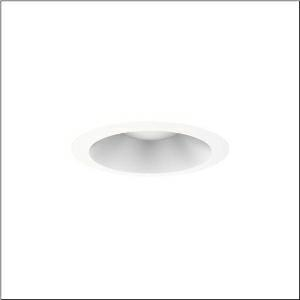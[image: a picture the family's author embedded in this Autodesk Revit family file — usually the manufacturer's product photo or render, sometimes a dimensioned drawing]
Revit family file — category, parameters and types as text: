
# Revit family: lunis_31-xl_51dn15eg42b
name_source: partatom
category: Lighting Fixtures
units: mm (PartAtom-declared; Revit-internal decimal feet)

## family parameters
Cut with Voids When Loaded = No
Host = Face
Light Source = No
Part Type = Normal
Room Calculation Point = No
Round Connector Dimension = Use Diameter
Shared = No

## types (1)
- --- (1 x LED, 2500 lm, 17.5 W, 4000K)
    Apparent Load = 18 VA
    CIE Flux Codes = 89 99 100 100 100
    Color Rendering = 80
    Color Temperature = 4000K
    Default Elevation = 1800 mm
    Description = Lunis 31-XL, downlight, light control with lens, light emission: direct distribution, LED rated luminous flux: 2.500lm, light colour: 840, mains connection: 220..240V, AC/DC, 0/50..60Hz, housing, of aluminium, white, protection rating (complete): IP20, protection rating (on room side): IP54, insulation class (complete): insulation class II (safety insulation), certification: CE, ENEC, packaging unit: 1 piece
    Height = 0 mm  [stored 0 ft]
    Lamp = 1 x LED
    Lamp Light Flux = 2500 lm
    Lamp Power = 17.5 W
    Lamp count = 1
    Length = 259 mm
    Luminous efficacy = 143 lm/W
    Manufacturer = Siteco
    ModVariant = No
    Model = 51DN15EG42B
    Mounting Place = Ceiling
    Mounting Type = Recessed
    Number of Poles = 1
    OnlyDefault = Yes
    Power Factor = 1
    Product Name = Lunis 31-XL
    Product group = downlight
    ProductGroupID = 401
    Protection Class = Protection class II
    Protection Degree = IP 20
    RLX_Detail_Level = 1
    RLX_Emergency_Light_Flux = 0 lm
    RLX_Emergency_Type = 0
    RLX_Emergency_Type_DB = No
    RlxData = <blob elided: 24093 chars, md5=40f161b8>
    Socket = socket
    Standby Power = 0 W
    System Light Flux = 2500 lm
    System Power = 18 W
    Type Comments = individual setting: luminous flux: 100 % | (ON | OFF | ON) | 450 mA
    Type Image = l_1345915.jpg
    URL = http://relux.com
    VarID = @adj_029607
    Voltage = 0 V
    Weight = 0.00 kg
    Width = 0 mm  [stored 0 ft]

note: [stored X ft] marks values corroborated as IEEE doubles in the binary element streams (Revit-internal decimal feet)

## geometry (parser evidence)
native form markers: Blend x4, Sweep x11
no freeform markers — native parametric forms only
